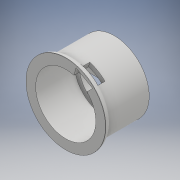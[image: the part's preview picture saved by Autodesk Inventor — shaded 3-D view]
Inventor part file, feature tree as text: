
AUTODESK INVENTOR PART (.ipt)
format: ipt  version: 2018 (Build 220112000, 112)  size: 218,112 bytes
history: native  units: mm
features: sketch x8, extrude x7, other x1, fillet x1
ambient origin geometry x8: Origin, YZ Plane, XZ Plane, XY Plane, X Axis, Y Axis, Z Axis, Center Point
bodies: Body1 (feature_tree)
feature tree (17):
  other  "Sólido1"
  extrude  "Extrusión1"  Depth=144.0mm
  extrude  "Extrusión2"  Depth=100.0mm TaperAngle=0.0deg
  extrude  "Extrusión3"  Depth=124.0mm
  extrude  "Extrusión4"  Depth=95.0mm
  fillet  "Empalme1"  Radius=124.0mm
  extrude  "Extrusión5"  Depth=80.0mm
  extrude  "Extrusión6"  Depth=15.0mm TaperAngle=0.0deg
  extrude  "Extrusión7"  Depth=15.0mm
  sketch  "Boceto11"  dims[d26=30.0mm d27=0.0mm d30=10.0mm d31=0.0mm d32=8.0mm d33=0.0mm]
  sketch  "Boceto1"  dims[d5=124.0mm d6=144.0mm]
  sketch  "Boceto5"  dims[d7=104.0mm d8=100.0mm d9=0.0mm]
  sketch  "Boceto6"  dims[d11=104.0mm d12=124.0mm]
  sketch  "Boceto7"  dims[d13=95.0mm d14=0.0mm d15=104.0mm d16=124.0mm]
  sketch  "Boceto8"  dims[d17=80.0mm d18=0.0mm d19=164.0mm]
  sketch  "Boceto9"  dims[d20=144.0mm d21=15.0mm d22=0.0mm]
  sketch  "Boceto10"  dims[d23=15.0mm d25=124.0mm]
